# Revit family: Haworth_Enclose_Wall_SolidTransom
name_source: partatom
category: Furniture Systems
revit_build: Autodesk Revit 2018 (Build: 20170223_1515(x64)
units: mm (PartAtom-declared; Revit-internal decimal feet)

## family parameters
Always vertical = Yes
Cut with Voids When Loaded = No
OmniClass Number = 23.25.40.14
OmniClass Title = Demountable Partitions
Part Type = Normal
Room Calculation Point = No
Round Connector Dimension = Use Diameter
Shared = Yes
Work Plane-Based = No

## types (5) — shared parameters
# of Panels Back = 3
# of Panels Front = 3
AFF Solid Panel Height = 88 "
Actual # of Panels Back = 3
Actual # of Panels Front = 3
Actual Height = 108 "
Actual Panel 1 Back Height = 32 "
Actual Panel 1 Front Height = 32 "
Actual Panel 2 Back Height = 64 "
Actual Panel 2 Front Height = 64 "
Actual Solid Panel Height = 88 "
Assembly Code = C1010200
Base Height = 1.25 "
Cap Height = 1 "
Ceiling Mount = Yes
Description = Wall - Solid Transom
End of Run Finish = Haworth _ Polymer _ Black
End of Run Width = 0.155 "
Frame Depth = 4 "
Frame Finish = Haworth _ Metal _ Brushed Aluminum
Glass Finish = Haworth _ Glass _ Clear
Glass Offset = 4.745 "
Glass Panel Depth = 0.4 "
Height = 108 "
Horizontal Bottom Adjuster Width = 3.87 "
Horizontal Bottom Trim Width = 2.425 "
Horizontal Frame Width = 0.875 "
Horizontal Top Adjuster Width = 2.625 "
Horizontal Top Trim Width = 1.43 "
Horizontal Transom Frame Width = 1.625 "
Manufacturer = Haworth
Material Options = http://surfaces.haworth.com
Max # of Panels = 3
Max. Height = 144 "
Max. Width = 60 "
Min. Height = 92 "
Min. Width = 8 "
Min/Max Height = 92-144 in.
Min/Max Width = 8-60 in.
Model = Haworth - Enclose
Offset Back = 9.84 "
Offset Front = 9.84 "
PH1B = 78.16 "
PH1F = 78.16 "
Panel 1 Back Height = 32 "
Panel 1 Front Height = 32 "
Panel 2 Back Height = 64 "
Panel 2 Front Height = 64 "
Panel Depth = 0.5 "
Panel Height 2 = 14.875 "
Panel Height Note = All Heights are A.F.F.
Panel Size Note = 8in increments
Raceway Finish = Haworth _ Metal _ Brushed Aluminum
Raceway Panel Back = Yes
Raceway Panel Back Height = 8.59 "
Raceway Panel Front = Yes
Raceway Panel Front Height = 8.59 "
Revision Number = 3
Size = Verify Final Dim. w/ Haworth
Sustainability Info = http://www.haworth.com
Transom Panel Height = 20 "
URL = www.haworth.com
URL - Product = http://www.haworth.com
Vertical Frame Width = 0.875 "
Warranty = http://www.haworth.com

## per-type parameters (varying)
| type | Actual Width | Panel Width 1 | Panel Width 2 | Raceway Panel Width | Width |
| 36" x 108" | 36 " | 35.69 " | 33.94 " | 35.69 " | 36 " |
| 24" x 108" | 24 " | 23.69 " | 21.94 " | 23.69 " | 24 " |
| 30" x 108" | 30 " | 29.69 " | 27.94 " | 29.69 " | 30 " |
| 42" x 108" | 42 " | 41.69 " | 39.94 " | 41.69 " | 42 " |
| 48" x 108" | 48 " | 47.69 " | 45.94 " | 47.69 " | 48 " |

## geometry (parser evidence)
native form markers: Sweep x13
no freeform markers — native parametric forms only
